# Revit family: Foundation-Barrier-StegoCrawl-Wrap-Vapor_Barrier-15mils
name_source: partatom
category: Specialty Equipment
units: mm (PartAtom-declared; Revit-internal decimal feet)

## family parameters
Cut with Voids When Loaded = No
Host = Face
OmniClass Number = 23.25.05.21
OmniClass Title = Special Foundations
Part Type = Normal
Room Calculation Point = No
Round Connector Dimension = Use Diameter
Shared = No

## types (2) — shared parameters
BIMobject category = Waterproofing & Membranes
Brand url = http://www.stegoindustries.com
Date of publishing = 8/16/2017
Default Elevation = 0' - 0"
Design country = United States
Edition number = 1
Installation instructions = https://www.stegoindustries.com
Low Emitting Material = Yes
Manufacturer = Stego Industries, LLC
Manufacturer country = United States
Manufacturer name = Stego Industries, LLC
Masterformat 2014 Code = 07 26 00
Masterformat 2014 Description = Vapor Retarders
Material main = Polyethylene
Nominal height = 0' - 0"
Nominal width = 0' - 0"
Product Documentation Link = https://www.stegoindustries.com
Product Guid = 1772a7ce-c4bf-4fda-9263-4d059c3fc038
Product Page URL = https://www.stegoindustries.com
Product certification = https://www.stegoindustries.com
Product data url = https://bimobject.com
Product family = Thermal and Moisture Protective Products
Product group = StegoCrawl Wrap
Product url = https://www.stegoindustries.com
QR code = http://bimobject.com
Technical description = Crawl Space Vapor Barrier
URL = http://www.stegoindustries.com
Vapor Barrier Thickness = 15 mils
Weight Net (Kg) = 0
Youtube clip = https://www.youtube.com

## per-type parameters (varying)
| type | ASTM | Description | Max Length Note | Model | Product SKU | Stego Vapor Barrier |
| StegoCrawl® Wrap Vapor Barrier 15 mils | Meets ASTM E1745 Requirements | StegoCrawl® Wrap Vapor Barrier utilizes the same industry-leading technology as Stego Wrap Vapor Barrier, but is specifically created for use in crawl spaces.  StegoCrawl Wrap 15-Mil Vapor Barrier is a Class I vapor retarder as defined by the 2009 IRC R601.3, and it is used to encapsulate crawl space floors and walls to protect the building envelope from moisture vapor and soil gas transmission.  StegoCrawl Wrap is a multi-layer plastic extrusion manufactured with only the highest grade of prime, virgin polyolefin resins. | Maximum roll length is 100'. | StegoCrawl® Wrap Vapor Barrier (15 mils) 1233 | stego005 | <By Category> |
| StegoCrawl® Wrap Perimeter Vapor Barrier 15 mils | Meets ASTM E1745 Requirements
Meets ASTM E1745 Requirements
Meets ASTM E1745 Requirements | StegoCrawl® Wrap Perimeter Vapor Barrier utilizes the same industry-leading technology as Stego Wrap Vapor Barrier, but is specifically created for use in crawl spaces. StegoCrawl Wrap 15-Mil Vapor Barrier is a Class I vapor retarder as defined by the 2009 IRC R601.3, and it is used to encapsulate crawl space floors and walls to protect the building envelope from moisture vapor and soil gas transmission.  StegoCrawl Wrap is a multi-layer plastic extrusion manufactured with only the highest grade of prime, virgin polyolefin resins.  This product is 14' x 100' -- a lighter, easier-to-carry roll than our commercial-grade rolls for horizontal placement. | Maximum roll length is 200'. | StegoCrawl® Wrap Perimeter Vapor Barrier (15 mils) 2468 | stego007 | StegoCrawl® Wrap Vapor Barrier - 15 mils |

## geometry (parser evidence)
native form markers: Sweep x2
no freeform markers — native parametric forms only
